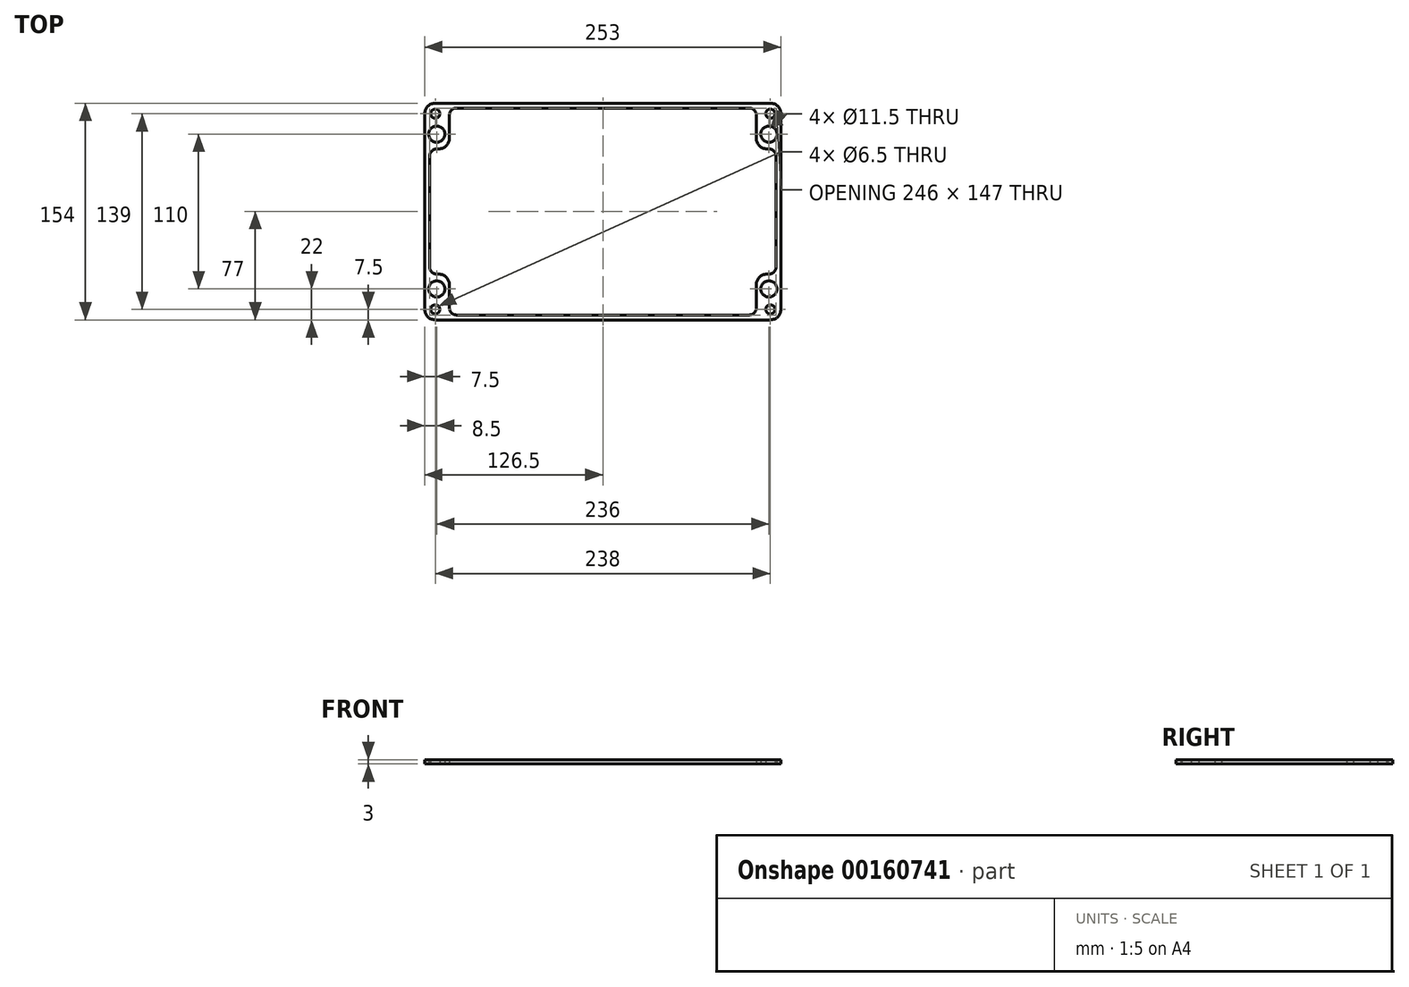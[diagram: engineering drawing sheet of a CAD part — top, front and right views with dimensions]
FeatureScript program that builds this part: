
annotation { "Feature Type Name" : "Feature", "Feature Type Description" : "" }
export const myFeature = defineFeature(function(context is Context, id is Id, definition is map)
    precondition{}
    {
        {
            var Q0;
            Q0=qCreatedBy(makeId("Top.planeOp"),FACE);
            var sketch = newSketch(context, id + "F0", { "sketchPlane" : qUnion([Q0])});
            skLineSegment(sketch, "E0.top", {"start": v(0, 77) * mm, "end": v(-119, 77) * mm});
            skLineSegment(sketch, "E0.right", {"start": v(-126.5, 0) * mm, "end": v(-126.5, 69.5) * mm});
            skPoint(sketch, "E0.middle", {"position": v(0, 0) * mm});
            skLineSegment(sketch, "E1.0", {"start": v(0, 73.5) * mm, "end": v(-104, 73.5) * mm});
            skLineSegment(sketch, "E1.3", {"start": v(-123, 0) * mm, "end": v(-123, 39.5) * mm});
            skLineSegment(sketch, "E2", {"start": v(-109, 68.5) * mm, "end": v(-109, 52) * mm});
            skLineSegment(sketch, "E3", {"start": v(-116.5, 44.5) * mm, "end": v(-118, 44.5) * mm});
            skLineSegment(sketch, "E4", {"start": v(0, 0) * mm, "end": v(0, 77) * mm, "construction": true});
            skLineSegment(sketch, "E5", {"start": v(-126.5, 0) * mm, "end": v(0, 0) * mm, "construction": true});
            skCircle(sketch, "E6", {"center": v(-118, 55) * mm, "radius": 5.75 * mm});
            skCircle(sketch, "E7", {"center": v(-119, 69.5) * mm, "radius": 3.25 * mm});
            skPoint(sketch, "E8.visualSharp", {"position": v(-126.5, 77) * mm});
            skArc(sketch, "E8.filletArc", {"start": v(-119, 77) * mm, "mid": v(-124.3, 74.8) * mm, "end": v(-126.5, 69.5) * mm});
            skPoint(sketch, "E9.visualSharp", {"position": v(-109, 44.5) * mm});
            skArc(sketch, "E9.filletArc", {"start": v(-116.5, 44.5) * mm, "mid": v(-111.2, 46.7) * mm, "end": v(-109, 52) * mm});
            skPoint(sketch, "E10.visualSharp", {"position": v(-123, 44.5) * mm});
            skArc(sketch, "E10.filletArc", {"start": v(-118, 44.5) * mm, "mid": v(-121.54, 43.04) * mm, "end": v(-123, 39.5) * mm});
            skPoint(sketch, "E11.visualSharp", {"position": v(-109, 73.5) * mm});
            skArc(sketch, "E11.filletArc", {"start": v(-104, 73.5) * mm, "mid": v(-107.54, 72.04) * mm, "end": v(-109, 68.5) * mm});
            skLineSegment(sketch, "E12.MirrorCS", {"start": v(116.5, 44.5) * mm, "end": v(118, 44.5) * mm});
            skArc(sketch, "E13.MirrorCS", {"start": v(104, 73.5) * mm, "mid": v(107.54, 72.04) * mm, "end": v(109, 68.5) * mm});
            skArc(sketch, "E14.MirrorCS", {"start": v(119, 77) * mm, "mid": v(124.3, 74.8) * mm, "end": v(126.5, 69.5) * mm});
            skArc(sketch, "E15.MirrorCS", {"start": v(118, 44.5) * mm, "mid": v(121.54, 43.04) * mm, "end": v(123, 39.5) * mm});
            skArc(sketch, "E16.MirrorCS", {"start": v(116.5, 44.5) * mm, "mid": v(111.2, 46.7) * mm, "end": v(109, 52) * mm});
            skPoint(sketch, "E17.MirrorP", {"position": v(126.5, 77) * mm});
            skPoint(sketch, "E18.MirrorP", {"position": v(123, 44.5) * mm});
            skLineSegment(sketch, "E19.MirrorCS", {"start": v(109, 68.5) * mm, "end": v(109, 52) * mm});
            skLineSegment(sketch, "E20.MirrorCS", {"start": v(123, 0) * mm, "end": v(123, 39.5) * mm});
            skLineSegment(sketch, "E21.MirrorCS", {"start": v(0, 73.5) * mm, "end": v(104, 73.5) * mm});
            skLineSegment(sketch, "E22.MirrorCS", {"start": v(0, 77) * mm, "end": v(119, 77) * mm});
            skCircle(sketch, "E23.MirrorC", {"center": v(118, 55) * mm, "radius": 5.75 * mm});
            skPoint(sketch, "E24.MirrorP", {"position": v(109, 73.5) * mm});
            skLineSegment(sketch, "E25.MirrorCS", {"start": v(126.5, 0) * mm, "end": v(126.5, 69.5) * mm});
            skCircle(sketch, "E26.MirrorC", {"center": v(119, 69.5) * mm, "radius": 3.25 * mm});
            skPoint(sketch, "E27.MirrorP", {"position": v(109, 44.5) * mm});
            skLineSegment(sketch, "E28.MirrorCS", {"start": v(126.5, 0) * mm, "end": v(0, 0) * mm, "construction": true});
            skLineSegment(sketch, "E29.MirrorCS", {"start": v(-116.5, -44.5) * mm, "end": v(-118, -44.5) * mm});
            skArc(sketch, "E30.MirrorCS", {"start": v(-104, -73.5) * mm, "mid": v(-107.54, -72.04) * mm, "end": v(-109, -68.5) * mm});
            skLineSegment(sketch, "E31.MirrorCS", {"start": v(116.5, -44.5) * mm, "end": v(118, -44.5) * mm});
            skArc(sketch, "E32.MirrorCS", {"start": v(119, -77) * mm, "mid": v(124.3, -74.8) * mm, "end": v(126.5, -69.5) * mm});
            skArc(sketch, "E33.MirrorCS", {"start": v(116.5, -44.5) * mm, "mid": v(111.2, -46.7) * mm, "end": v(109, -52) * mm});
            skArc(sketch, "E34.MirrorCS", {"start": v(-118, -44.5) * mm, "mid": v(-121.54, -43.04) * mm, "end": v(-123, -39.5) * mm});
            skArc(sketch, "E35.MirrorCS", {"start": v(-116.5, -44.5) * mm, "mid": v(-111.2, -46.7) * mm, "end": v(-109, -52) * mm});
            skArc(sketch, "E36.MirrorCS", {"start": v(-119, -77) * mm, "mid": v(-124.3, -74.8) * mm, "end": v(-126.5, -69.5) * mm});
            skArc(sketch, "E37.MirrorCS", {"start": v(104, -73.5) * mm, "mid": v(107.54, -72.04) * mm, "end": v(109, -68.5) * mm});
            skArc(sketch, "E38.MirrorCS", {"start": v(118, -44.5) * mm, "mid": v(121.54, -43.04) * mm, "end": v(123, -39.5) * mm});
            skPoint(sketch, "E39.MirrorP", {"position": v(-109, -73.5) * mm});
            skLineSegment(sketch, "E40.MirrorCS", {"start": v(123, 0) * mm, "end": v(123, -39.5) * mm});
            skLineSegment(sketch, "E41.MirrorCS", {"start": v(0, -77) * mm, "end": v(119, -77) * mm});
            skCircle(sketch, "E42.MirrorC", {"center": v(118, -55) * mm, "radius": 5.75 * mm});
            skCircle(sketch, "E43.MirrorC", {"center": v(119, -69.5) * mm, "radius": 3.25 * mm});
            skCircle(sketch, "E44.MirrorC", {"center": v(-119, -69.5) * mm, "radius": 3.25 * mm});
            skCircle(sketch, "E45.MirrorC", {"center": v(-118, -55) * mm, "radius": 5.75 * mm});
            skLineSegment(sketch, "E46.MirrorCS", {"start": v(0, 0) * mm, "end": v(0, -77) * mm, "construction": true});
            skLineSegment(sketch, "E47.MirrorCS", {"start": v(-109, -68.5) * mm, "end": v(-109, -52) * mm});
            skLineSegment(sketch, "E48.MirrorCS", {"start": v(-123, 0) * mm, "end": v(-123, -39.5) * mm});
            skLineSegment(sketch, "E49.MirrorCS", {"start": v(0, -73.5) * mm, "end": v(-104, -73.5) * mm});
            skPoint(sketch, "E50.MirrorP", {"position": v(126.5, -77) * mm});
            skLineSegment(sketch, "E51.MirrorCS", {"start": v(0, -77) * mm, "end": v(-119, -77) * mm});
            skPoint(sketch, "E52.MirrorP", {"position": v(-123, -44.5) * mm});
            skLineSegment(sketch, "E53.MirrorCS", {"start": v(-126.5, 0) * mm, "end": v(-126.5, -69.5) * mm});
            skPoint(sketch, "E54.MirrorP", {"position": v(109, -73.5) * mm});
            skPoint(sketch, "E55.MirrorP", {"position": v(123, -44.5) * mm});
            skPoint(sketch, "E56.MirrorP", {"position": v(-126.5, -77) * mm});
            skLineSegment(sketch, "E57.MirrorCS", {"start": v(109, -68.5) * mm, "end": v(109, -52) * mm});
            skPoint(sketch, "E58.MirrorP", {"position": v(-109, -44.5) * mm});
            skLineSegment(sketch, "E59.MirrorCS", {"start": v(126.5, 0) * mm, "end": v(126.5, -69.5) * mm});
            skLineSegment(sketch, "E60.MirrorCS", {"start": v(0, -73.5) * mm, "end": v(104, -73.5) * mm});
            skPoint(sketch, "E61.MirrorP", {"position": v(109, -44.5) * mm});
            skSolve(sketch);
        }
        {
            var Q0;
            Q0=makeQuery(id+"F0.imprint","IMPRINT",FACE,{"disambiguationData":[TD([[makeQuery(id+"F0.imprint","IMPRINT",EDGE,{"derivedFrom":sQuery(id+"F0.wireOp",EDGE,"E0.top")}),1.0]])]});
            extrude(context, id + "F1", {"entities" : qUnion([Q0]), "depth" : 3 * mm});
        }
    });
